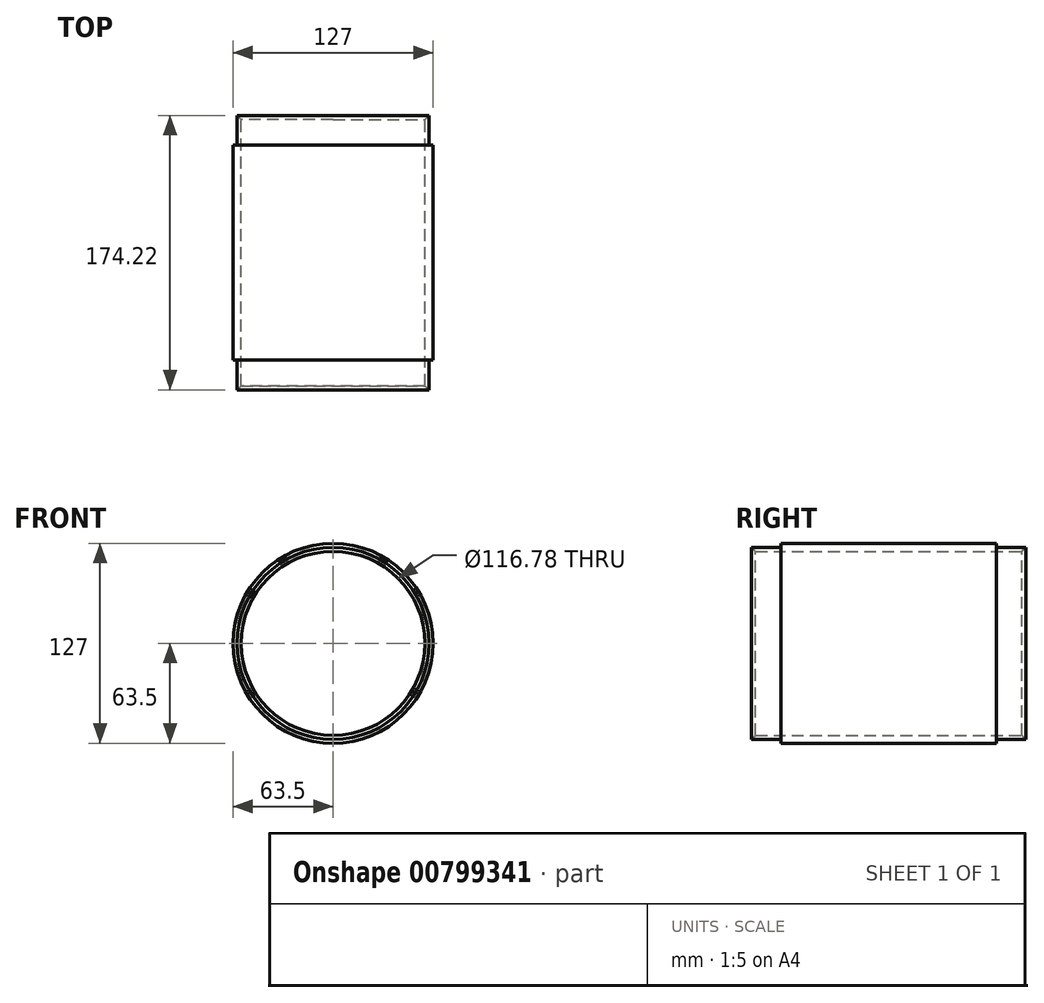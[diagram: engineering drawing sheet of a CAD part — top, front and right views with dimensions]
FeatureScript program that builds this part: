
annotation { "Feature Type Name" : "Feature", "Feature Type Description" : "" }
export const myFeature = defineFeature(function(context is Context, id is Id, definition is map)
    precondition{}
    {
        {
            var Q0;
            Q0=qCreatedBy(makeId("Front.planeOp"),FACE);
            var sketch = newSketch(context, id + "F0", { "sketchPlane" : qUnion([Q0])});
            skCircle(sketch, "E0", {"center": v(0, 0) * mm, "radius": 58.4 * mm});
            skCircle(sketch, "E1", {"center": v(0, 0) * mm, "radius": 63.5 * mm});
            skSolve(sketch);
        }
        {
            var Q0;
            Q0=makeQuery(id+"F0.imprint","IMPRINT",FACE,{"disambiguationData":[TD([[makeQuery(id+"F0.imprint","IMPRINT",EDGE,{"derivedFrom":sQuery(id+"F0.wireOp",EDGE,"E0")}),-1.0]])]});
            extrude(context, id + "F1", {"entities" : qUnion([Q0]), "depth" : 175 * mm});
        }
        {
            var Q0;
            Q0=qCreatedBy(makeId("Front.planeOp"),FACE);
            var sketch = newSketch(context, id + "F2", { "sketchPlane" : qUnion([Q0])});
            skCircle(sketch, "E2", {"center": v(0, 0) * mm, "radius": 61 * mm});
            skCircle(sketch, "E3", {"center": v(0, 0) * mm, "radius": 63.5 * mm});
            skSolve(sketch);
        }
        {
            var Q0;
            Q0=makeQuery(id+"F2.imprint","IMPRINT",FACE,{"disambiguationData":[TD([[makeQuery(id+"F2.imprint","IMPRINT",EDGE,{"derivedFrom":sQuery(id+"F2.wireOp",EDGE,"E2")}),-1.0]])]});
            extrude(context, id + "F3", {"entities" : qUnion([Q0]), "operationType" : NewBodyOperationType.REMOVE, "depth" : 19.2 * mm, "offsetDistance" : 25 * mm});
        }
        {
            var Q0;
            Q0=makeQuery(id+"F1.opExtrude","CAP_FACE",FACE,{"disambiguationData":[OSD([sQuery(id+"F0.wireOp",EDGE,"E0"),sQuery(id+"F0.wireOp",EDGE,"E1")])],"isStart":false});
            var sketch = newSketch(context, id + "F4", { "sketchPlane" : qUnion([Q0])});
            skCircle(sketch, "E4", {"center": v(0, 0) * mm, "radius": 61 * mm});
            skCircle(sketch, "E5", {"center": v(0, 0) * mm, "radius": 63.5 * mm});
            skSolve(sketch);
        }
        {
            var Q0;
            Q0=makeQuery(id+"F4.imprint","IMPRINT",FACE,{"disambiguationData":[TD([[makeQuery(id+"F4.imprint","IMPRINT",EDGE,{"derivedFrom":sQuery(id+"F4.wireOp",EDGE,"E4")}),-1.0]])]});
            extrude(context, id + "F5", {"entities" : qUnion([Q0]), "operationType" : NewBodyOperationType.REMOVE, "oppositeDirection" : true, "depth" : 19.2 * mm, "offsetDistance" : 25 * mm});
        }
        {
            var Q0;
            Q0=makeQuery(id+"F1.opExtrude","CAP_EDGE",EDGE,{"disambiguationData":[OSD([sQuery(id+"F0.wireOp",EDGE,"E0")])],"isStart":false});
            var Q1;
            Q1=makeQuery(id+"F1.opExtrude","CAP_EDGE",EDGE,{"disambiguationData":[OSD([sQuery(id+"F0.wireOp",EDGE,"E0")])],"isStart":true});
            chamfer(context, id + "F6", {"entities" : qUnion([Q0, Q1]), "width" : 3 * mm, "tangentPropagation" : true});
        }
    });
